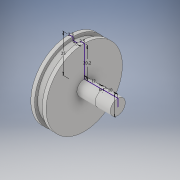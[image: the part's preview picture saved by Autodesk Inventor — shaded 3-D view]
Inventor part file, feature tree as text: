
AUTODESK INVENTOR PART (.ipt)
format: ipt  version: 2019 (Build 230136000, 136)  size: 126,976 bytes
history: native  units: in
note: dims shown in document units (in); Inventor stores cm internally (conversion verified against a paired STEP export)
features: revolve x1, sketch x1
ambient origin geometry x8: Origin, YZ Plane, XZ Plane, XY Plane, X Axis, Y Axis, Z Axis, Center Point
bodies: Solid1 (feature_tree)
feature tree (2):
  revolve  "Revolution1"  [1 undecoded]
  sketch  "Sketch1"  dims[d0=0.9843in d1=0.0984in d2=0.0787in d3=0.1969in d4=0.0984in d5=0.7953in d6=0.4724in d7=0.0039in d8=0.3937in d9=90.0deg d10=0.3858in]
note: 1 required parameter value undecoded (feature->parameter linkage not recoverable at this tier; creation-order binding heuristic only, values carry confidence <= 0.55)
